# Revit family: Poly-Max-Ceiling-Tiles
name_source: partatom
category: Specialty Equipment
units: mm (PartAtom-declared; Revit-internal decimal feet)

## family parameters
Always vertical = No
Cut with Voids When Loaded = No
Enable Cutting in Views = Yes
Maintain Annotation Orientation = No
OmniClass Number = 23.35.00.00
OmniClass Title = Covering, Cladding, and Finishes
Part Type = Normal
Room Calculation Point = No
Round Connector Dimension = Use Diameter
Shared = No
Work Plane-Based = Yes

## types (54) — shared parameters
A = 0' - 0"
Acoustics - NRC = Sound absorption varies from NRC 0.45 to 0.95 based on installation method used when tested per ASTM C423.
Assembly Code = C30
Default Elevation = 4' - 0"
Description = Acoustic Panels
Fire Rating = ASTM E84 - Class A
Manufacturer = Acoustical Surfaces, Inc.
Material = Poly Max
Model = Poly Max - Ceiling Panels
Recycled Content Percentage = 0%
Type Comments = Acoustic Panels
URL = https://www.acousticalsurfaces.com

## per-type parameters (varying)
| type | Finish | Length | T | Thickness Options | Width | ‍      0. Thickness 1/2" | ‍      1. Thickness 1" |
| 1 INCH THICK - 2x2 - White | Paint - Acoustical-Surfaces - White | 2' - 0" | 0' - 1" | 1 | 2' - 0" | No | Yes |
| 1 INCH THICK - 2x2 - Beige | Paint - Acoustical-Surfaces - Beige | 2' - 0" | 0' - 1" | 1 | 2' - 0" | No | Yes |
| 1 INCH THICK - 2x2- Silver | Paint - Acoustical-Surfaces - Silver | 2' - 0" | 0' - 1" | 1 | 2' - 0" | No | Yes |
| 1 INCH THICK - 2x2 - Black | Paint - Acoustical-Surfaces - Black | 2' - 0" | 0' - 1" | 1 | 2' - 0" | No | Yes |
| 1 INCH THICK - 2x2 - Printed Graphics | Paint - Acoustical-Surfaces - Printed Graphics | 2' - 0" | 0' - 1" | 1 | 2' - 0" | No | Yes |
| HALF INCH THICK - 2x2 - Orange | Paint - Acoustical-Surfaces - Orange | 2' - 0" | 0' - 0 1/2" | 0 | 2' - 0" | Yes | No |
| HALF INCH THICK - 2x2 - Grey | Paint - Acoustical-Surfaces - Grey | 2' - 0" | 0' - 0 1/2" | 0 | 2' - 0" | Yes | No |
| HALF INCH THICK - 2x2 -White | Paint - Acoustical-Surfaces - White | 2' - 0" | 0' - 0 1/2" | 0 | 2' - 0" | Yes | No |
| HALF INCH THICK - 2x2 - Black | Paint - Acoustical-Surfaces - Black | 2' - 0" | 0' - 0 1/2" | 0 | 2' - 0" | Yes | No |
| HALF INCH THICK - 2x2 - Beige | Paint - Acoustical-Surfaces - Beige | 2' - 0" | 0' - 0 1/2" | 0 | 2' - 0" | Yes | No |
| HALF INCH THICK - 2x2 - Printed Graphics | Paint - Acoustical-Surfaces - Printed Graphics | 2' - 0" | 0' - 0 1/2" | 0 | 2' - 0" | Yes | No |
| HALF INCH THICK - 2x2 - Blue | Paint - Acoustical-Surfaces - Blue | 2' - 0" | 0' - 0 1/2" | 0 | 2' - 0" | Yes | No |
| HALF INCH THICK - 2x2 - Tan | Paint - Acoustical-Surfaces - Tan | 2' - 0" | 0' - 0 1/2" | 0 | 2' - 0" | Yes | No |
| HALF INCH THICK - 2x2 - Purple | Paint - Acoustical-Surfaces - Purple | 2' - 0" | 0' - 0 1/2" | 0 | 2' - 0" | Yes | No |
| HALF INCH THICK - 2x2 - Brown | Paint - Acoustical-Surfaces - Brown | 2' - 0" | 0' - 0 1/2" | 0 | 2' - 0" | Yes | No |
| HALF INCH THICK - 2x2 - Red | Paint - Acoustical-Surfaces - Red | 2' - 0" | 0' - 0 1/2" | 0 | 2' - 0" | Yes | No |
| HALF INCH THICK - 2x2 - Silver | Paint - Acoustical-Surfaces - Silver | 2' - 0" | 0' - 0 1/2" | 0 | 2' - 0" | Yes | No |
| HALF INCH THICK - 4x8 - Printed Grpahics | Paint - Acoustical-Surfaces - Printed Graphics | 8' - 0" | 0' - 0 1/2" | 0 | 4' - 0" | Yes | No |
| HALF INCH THICK - 4x8 - Lime | Paint - Acoustical-Surfaces - Lime | 8' - 0" | 0' - 0 1/2" | 0 | 4' - 0" | Yes | No |
| HALF INCH THICK - 4x8 - Orange | Paint - Acoustical-Surfaces - Orange | 8' - 0" | 0' - 0 1/2" | 0 | 4' - 0" | Yes | No |
| HALF INCH THICK - 4x8 - Red | Paint - Acoustical-Surfaces - Red | 8' - 0" | 0' - 0 1/2" | 0 | 4' - 0" | Yes | No |
| HALF INCH THICK - 4x8 - Purple | Paint - Acoustical-Surfaces - Purple | 8' - 0" | 0' - 0 1/2" | 0 | 4' - 0" | Yes | No |
| HALF INCH THICK - 4x8 - Blue | Paint - Acoustical-Surfaces - Blue | 8' - 0" | 0' - 0 1/2" | 0 | 4' - 0" | Yes | No |
| HALF INCH THICK - 4x8 - Black | Paint - Acoustical-Surfaces - Black | 8' - 0" | 0' - 0 1/2" | 0 | 4' - 0" | Yes | No |
| HALF INCH THICK - 4x8 - Grey | Paint - Acoustical-Surfaces - Grey | 8' - 0" | 0' - 0 1/2" | 0 | 4' - 0" | Yes | No |
| HALF INCH THICK - 4x8 - Silver | Paint - Acoustical-Surfaces - Silver | 8' - 0" | 0' - 0 1/2" | 0 | 4' - 0" | Yes | No |
| HALF INCH THICK - 4x8 - Brown | Paint - Acoustical-Surfaces - Brown | 8' - 0" | 0' - 0 1/2" | 0 | 4' - 0" | Yes | No |
| HALF INCH THICK - 4x8 - Tan | Paint - Acoustical-Surfaces - Tan | 8' - 0" | 0' - 0 1/2" | 0 | 4' - 0" | Yes | No |
| HALF INCH THICK - 4x8 - Beige | Paint - Acoustical-Surfaces - Beige | 8' - 0" | 0' - 0 1/2" | 0 | 4' - 0" | Yes | No |
| HALF INCH THICK - 4x8 - White | Paint - Acoustical-Surfaces - White | 8' - 0" | 0' - 0 1/2" | 0 | 4' - 0" | Yes | No |
| HALF INCH THICK - 2x4 - Tan | Paint - Acoustical-Surfaces - Tan | 4' - 0" | 0' - 0 1/2" | 0 | 2' - 0" | Yes | No |
| HALF INCH THICK - 2x4 - Brown | Paint - Acoustical-Surfaces - Brown | 4' - 0" | 0' - 0 1/2" | 0 | 2' - 0" | Yes | No |
| HALF INCH THICK - 2x4 - Grey | Paint - Acoustical-Surfaces - Grey | 4' - 0" | 0' - 0 1/2" | 0 | 2' - 0" | Yes | No |
| HALF INCH THICK - 2x4 - Blue | Paint - Acoustical-Surfaces - Blue | 4' - 0" | 0' - 0 1/2" | 0 | 2' - 0" | Yes | No |
| HALF INCH THICK - 2x4 - Purple | Paint - Acoustical-Surfaces - Purple | 4' - 0" | 0' - 0 1/2" | 0 | 2' - 0" | Yes | No |
| HALF INCH THICK - 2x4 - Red | Paint - Acoustical-Surfaces - Red | 4' - 0" | 0' - 0 1/2" | 0 | 2' - 0" | Yes | No |
| HALF INCH THICK - 2x4 - Orange | Paint - Acoustical-Surfaces - Orange | 4' - 0" | 0' - 0 1/2" | 0 | 2' - 0" | Yes | No |
| HALF INCH THICK - 2x4 - Printed Graphics | Paint - Acoustical-Surfaces - Printed Graphics | 4' - 0" | 0' - 0 1/2" | 0 | 2' - 0" | Yes | No |
| HALF INCH THICK - 2x4 - Black | Paint - Acoustical-Surfaces - Black | 4' - 0" | 0' - 0 1/2" | 0 | 2' - 0" | Yes | No |
| HALF INCH THICK - 2x4 - Silver | Paint - Acoustical-Surfaces - Silver | 4' - 0" | 0' - 0 1/2" | 0 | 2' - 0" | Yes | No |
| HALF INCH THICK - 2x4 - Beige | Paint - Acoustical-Surfaces - Beige | 4' - 0" | 0' - 0 1/2" | 0 | 2' - 0" | Yes | No |
| 1 INCH THICK - 4x8 - Printed Grpahics | Paint - Acoustical-Surfaces - Printed Graphics | 8' - 0" | 0' - 1" | 1 | 4' - 0" | No | Yes |
| 1 INCH THICK - 4x8 - Silver | Paint - Acoustical-Surfaces - Silver | 8' - 0" | 0' - 1" | 1 | 4' - 0" | No | Yes |
| 1 INCH THICK - 4x8 - Black | Paint - Acoustical-Surfaces - Black | 8' - 0" | 0' - 1" | 1 | 4' - 0" | No | Yes |
| 1 INCH THICK - 4x8 - White | Paint - Acoustical-Surfaces - White | 8' - 0" | 0' - 1" | 1 | 4' - 0" | No | Yes |
| 1 INCH THICK - 2x4- Silver | Paint - Acoustical-Surfaces - Silver | 4' - 0" | 0' - 1" | 1 | 2' - 0" | No | Yes |
| 1 INCH THICK - 2x4 - Black | Paint - Acoustical-Surfaces - Black | 4' - 0" | 0' - 1" | 1 | 2' - 0" | No | Yes |
| 1 INCH THICK - 2x4 - Beige | Paint - Acoustical-Surfaces - Beige | 4' - 0" | 0' - 1" | 1 | 2' - 0" | No | Yes |
| 1 INCH THICK - 2x4 - White | Paint - Acoustical-Surfaces - White | 4' - 0" | 0' - 1" | 1 | 2' - 0" | No | Yes |
| 1 INCH THICK - 2x4 - Printed Graphics | Paint - Acoustical-Surfaces - Printed Graphics | 4' - 0" | 0' - 1" | 1 | 2' - 0" | No | Yes |
| HALF INCH THICK - 2x2 - Lime | Paint - Acoustical-Surfaces - Lime | 2' - 0" | 0' - 0 1/2" | 0 | 2' - 0" | Yes | No |
| HALF INCH THICK - 2x4 - Lime | Paint - Acoustical-Surfaces - Lime | 4' - 0" | 0' - 0 1/2" | 0 | 2' - 0" | Yes | No |
| HALF INCH THICK - 2x4 - White | Paint - Acoustical-Surfaces - White | 4' - 0" | 0' - 0 1/2" | 0 | 2' - 0" | Yes | No |
| 1 INCH THICK - 4x8 - Beige | Paint - Acoustical-Surfaces - Beige | 8' - 0" | 0' - 1" | 1 | 4' - 0" | No | Yes |

## geometry (parser evidence)
native form markers: Sweep x11
no freeform markers — native parametric forms only
